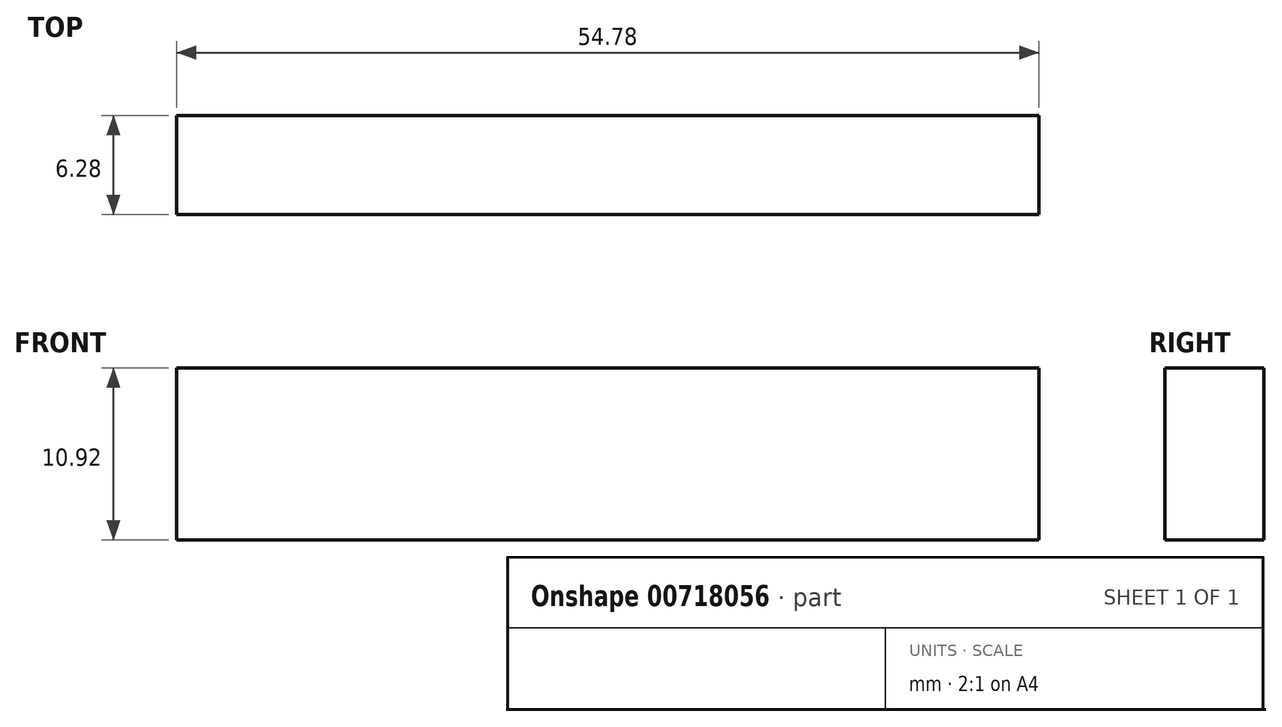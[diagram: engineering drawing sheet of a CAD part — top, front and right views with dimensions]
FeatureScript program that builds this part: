
annotation { "Feature Type Name" : "Feature", "Feature Type Description" : "" }
export const myFeature = defineFeature(function(context is Context, id is Id, definition is map)
    precondition{}
    {
        {
            var Q0;
            Q0=qCreatedBy(makeId("Front.planeOp"),FACE);
            var sketch = newSketch(context, id + "F0", { "sketchPlane" : qUnion([Q0])});
            skLineSegment(sketch, "E0.bottom", {"start": v(0, 0) * mm, "end": v(95.63, 0) * mm});
            skLineSegment(sketch, "E0.top", {"start": v(0, 97.83) * mm, "end": v(95.63, 97.83) * mm});
            skLineSegment(sketch, "E0.left", {"start": v(0, 0) * mm, "end": v(0, 97.83) * mm});
            skLineSegment(sketch, "E0.right", {"start": v(95.63, 0) * mm, "end": v(95.63, 97.83) * mm});
            skLineSegment(sketch, "E1.bottom", {"start": v(0, 97.83) * mm, "end": v(-94.65, 97.83) * mm});
            skLineSegment(sketch, "E1.top", {"start": v(0, -95.54) * mm, "end": v(-94.65, -95.54) * mm});
            skLineSegment(sketch, "E1.left", {"start": v(0, 97.83) * mm, "end": v(0, -95.54) * mm});
            skLineSegment(sketch, "E1.right", {"start": v(-94.65, 97.83) * mm, "end": v(-94.65, -95.54) * mm});
            skLineSegment(sketch, "E2.bottom", {"start": v(0, -95.54) * mm, "end": v(95.63, -95.54) * mm});
            skLineSegment(sketch, "E2.left", {"start": v(0, -95.54) * mm, "end": v(0, 0) * mm});
            skLineSegment(sketch, "E2.right", {"start": v(95.63, -95.54) * mm, "end": v(95.63, 0) * mm});
            skLineSegment(sketch, "E3.bottom", {"start": v(-34.5, 130.58) * mm, "end": v(16.55, 130.58) * mm});
            skLineSegment(sketch, "E3.top", {"start": v(-34.5, -108.24) * mm, "end": v(16.55, -108.24) * mm});
            skLineSegment(sketch, "E3.left", {"start": v(-34.5, 130.58) * mm, "end": v(-34.5, -108.24) * mm});
            skLineSegment(sketch, "E3.right", {"start": v(16.55, 130.58) * mm, "end": v(16.55, -108.24) * mm});
            skLineSegment(sketch, "E4.bottom", {"start": v(16.55, 130.58) * mm, "end": v(149.66, 130.58) * mm});
            skLineSegment(sketch, "E4.top", {"start": v(16.55, -99) * mm, "end": v(149.66, -99) * mm});
            skLineSegment(sketch, "E4.left", {"start": v(16.55, 130.58) * mm, "end": v(16.55, -99) * mm});
            skLineSegment(sketch, "E4.right", {"start": v(149.66, 130.58) * mm, "end": v(149.66, -99) * mm});
            skLineSegment(sketch, "E5.bottom", {"start": v(-34.5, -95.54) * mm, "end": v(-151.3, -95.54) * mm});
            skLineSegment(sketch, "E5.top", {"start": v(-34.5, 120.83) * mm, "end": v(-151.3, 120.83) * mm});
            skLineSegment(sketch, "E5.left", {"start": v(-34.5, -95.54) * mm, "end": v(-34.5, 120.83) * mm});
            skLineSegment(sketch, "E5.right", {"start": v(-151.3, -95.54) * mm, "end": v(-151.3, 120.83) * mm});
            skSolve(sketch);
        }
        {
            var Q0;
            Q0 = qSketchRegion(id + "F0", true);
            extrude(context, id + "F1", {"entities" : qUnion([Q0]), "depth" : 25.4 * mm, "offsetDistance" : 25.4 * mm});
        }
        {
            var Q0;
            Q0=makeQuery(id+"F1.opExtrude","CAP_FACE",FACE,{"disambiguationData":[OSD([sQuery(id+"F0.wireOp",EDGE,"E0.top"),sQuery(id+"F0.wireOp",EDGE,"E0.right"),sQuery(id+"F0.wireOp",EDGE,"E1.left"),sQuery(id+"F0.wireOp",EDGE,"E2.bottom"),sQuery(id+"F0.wireOp",EDGE,"E2.left"),sQuery(id+"F0.wireOp",EDGE,"E2.right"),sQuery(id+"F0.wireOp",EDGE,"E3.bottom"),sQuery(id+"F0.wireOp",EDGE,"E3.top"),sQuery(id+"F0.wireOp",EDGE,"E3.left"),sQuery(id+"F0.wireOp",EDGE,"E3.right"),sQuery(id+"F0.wireOp",EDGE,"E4.bottom"),sQuery(id+"F0.wireOp",EDGE,"E4.top"),sQuery(id+"F0.wireOp",EDGE,"E4.right"),sQuery(id+"F0.wireOp",EDGE,"E5.bottom"),sQuery(id+"F0.wireOp",EDGE,"E5.top"),sQuery(id+"F0.wireOp",EDGE,"E5.right")])],"isStart":true});
            var sketch = newSketch(context, id + "F2", { "sketchPlane" : qUnion([Q0])});
            skLineSegment(sketch, "E6.bottom", {"start": v(-95.63, 108.88) * mm, "end": v(291.77, 108.88) * mm});
            skLineSegment(sketch, "E6.top", {"start": v(-95.63, -277) * mm, "end": v(291.77, -277) * mm});
            skLineSegment(sketch, "E6.left", {"start": v(-95.63, 108.88) * mm, "end": v(-95.63, -277) * mm});
            skLineSegment(sketch, "E6.right", {"start": v(291.77, 108.88) * mm, "end": v(291.77, -277) * mm});
            skPoint(sketch, "E6.middle", {"position": v(98.07, -84.06) * mm});
            skSolve(sketch);
        }
        {
            var Q0;
            {var subQ13=makeQuery(id+"F1.opExtrude","CAP_EDGE",EDGE,{"disambiguationData":[OSD([sQuery(id+"F0.wireOp",EDGE,"E0.top")])],"isStart":true});Q0=makeQuery(id+"F2.imprint","IMPRINT",FACE,{"disambiguationData":[TD([[makeQuery(id+"F2.imprint","IMPRINT",EDGE,{"derivedFrom":subQ13}),-1.0]])]});}
            var Q1;
            {var subQ1=makeQuery(id+"F1.opExtrude","CAP_EDGE",EDGE,{"disambiguationData":[OSD([sQuery(id+"F0.wireOp",EDGE,"E0.top")])],"isStart":true});Q1=makeQuery(id+"F2.imprint","IMPRINT",FACE,{"disambiguationData":[TD([[makeQuery(id+"F2.imprint","IMPRINT",EDGE,{"derivedFrom":subQ1}),1.0]])]});}
            extrude(context, id + "F3", {"entities" : qUnion([Q0, Q1]), "operationType" : NewBodyOperationType.ADD, "oppositeDirection" : true, "depth" : 346.17 * mm, "offsetDistance" : 25.4 * mm});
        }
        {
            var Q0;
            {var subQ0=sQuery(id+"F0.wireOp",EDGE,"E5.right");var subQ1=sQuery(id+"F0.wireOp",EDGE,"E5.bottom");var subQ2=sQuery(id+"F0.wireOp",EDGE,"E4.top");var subQ3=sQuery(id+"F0.wireOp",EDGE,"E3.right");var subQ4=sQuery(id+"F0.wireOp",EDGE,"E3.left");var subQ5=sQuery(id+"F0.wireOp",EDGE,"E3.top");Q0=makeQuery(id+"F3.boolean.opBoolean","MERGE",FACE,{"derivedFrom":[makeQuery(id+"F1.opExtrude","CAP_FACE",FACE,{"disambiguationData":[OSD([sQuery(id+"F0.wireOp",EDGE,"E0.top"),sQuery(id+"F0.wireOp",EDGE,"E0.right"),sQuery(id+"F0.wireOp",EDGE,"E1.left"),sQuery(id+"F0.wireOp",EDGE,"E2.bottom"),sQuery(id+"F0.wireOp",EDGE,"E2.left"),sQuery(id+"F0.wireOp",EDGE,"E2.right"),sQuery(id+"F0.wireOp",EDGE,"E3.bottom"),subQ5,subQ4,subQ3,sQuery(id+"F0.wireOp",EDGE,"E4.bottom"),subQ2,sQuery(id+"F0.wireOp",EDGE,"E4.right"),subQ1,sQuery(id+"F0.wireOp",EDGE,"E5.top"),subQ0])],"isStart":true}),makeQuery(id+"F3.opExtrude","CAP_FACE",FACE,{"disambiguationData":[OSD([subQ5,subQ4,subQ3,subQ2,subQ1,subQ0,sQuery(id+"F2.wireOp",EDGE,"E6.bottom"),sQuery(id+"F2.wireOp",EDGE,"E6.left")])],"isStart":true})]});}
            var sketch = newSketch(context, id + "F4", { "sketchPlane" : qUnion([Q0])});
            skLineSegment(sketch, "E7.bottom", {"start": v(-77.36, 89.2) * mm, "end": v(78.88, 89.2) * mm});
            skLineSegment(sketch, "E7.top", {"start": v(-77.36, -67.08) * mm, "end": v(78.88, -67.08) * mm});
            skLineSegment(sketch, "E7.left", {"start": v(-77.36, 89.2) * mm, "end": v(-77.36, -67.08) * mm});
            skLineSegment(sketch, "E7.right", {"start": v(78.88, 89.2) * mm, "end": v(78.88, -67.08) * mm});
            skLineSegment(sketch, "E8.bottom", {"start": v(-113.4, 15.53) * mm, "end": v(-77.36, 15.53) * mm});
            skLineSegment(sketch, "E8.top", {"start": v(-113.4, 43.9) * mm, "end": v(-77.36, 43.9) * mm});
            skLineSegment(sketch, "E8.left", {"start": v(-113.4, 15.53) * mm, "end": v(-113.4, 43.9) * mm});
            skLineSegment(sketch, "E8.right", {"start": v(-77.36, 15.53) * mm, "end": v(-77.36, 43.9) * mm});
            skLineSegment(sketch, "E9.top", {"start": v(-113.4, -26.5) * mm, "end": v(-77.36, -26.5) * mm});
            skLineSegment(sketch, "E9.left", {"start": v(-113.4, 15.53) * mm, "end": v(-113.4, -26.5) * mm});
            skLineSegment(sketch, "E9.right", {"start": v(-77.36, 15.53) * mm, "end": v(-77.36, -26.5) * mm});
            skLineSegment(sketch, "E10.top", {"start": v(-113.4, -67.08) * mm, "end": v(-77.36, -67.08) * mm});
            skLineSegment(sketch, "E10.left", {"start": v(-113.4, -26.5) * mm, "end": v(-113.4, -67.08) * mm});
            skLineSegment(sketch, "E10.right", {"start": v(-77.36, -26.5) * mm, "end": v(-77.36, -67.08) * mm});
            skLineSegment(sketch, "E11.top", {"start": v(-113.4, 89.2) * mm, "end": v(-77.36, 89.2) * mm});
            skLineSegment(sketch, "E11.left", {"start": v(-113.4, 43.9) * mm, "end": v(-113.4, 89.2) * mm});
            skLineSegment(sketch, "E11.right", {"start": v(-77.36, 43.9) * mm, "end": v(-77.36, 89.2) * mm});
            skSolve(sketch);
        }
        {
            var Q0;
            Q0 = qSketchRegion(id + "F4", true);
            extrude(context, id + "F5", {"entities" : qUnion([Q0]), "operationType" : NewBodyOperationType.ADD, "depth" : 25.4 * mm, "offsetDistance" : 25.4 * mm});
        }
        {
            var Q0;
            Q0=makeQuery(id+"F5.opExtrude","CAP_FACE",FACE,{"disambiguationData":[OSD([sQuery(id+"F4.wireOp",EDGE,"E7.bottom"),sQuery(id+"F4.wireOp",EDGE,"E7.top"),sQuery(id+"F4.wireOp",EDGE,"E7.right"),sQuery(id+"F4.wireOp",EDGE,"E8.left"),sQuery(id+"F4.wireOp",EDGE,"E9.left"),sQuery(id+"F4.wireOp",EDGE,"E10.top"),sQuery(id+"F4.wireOp",EDGE,"E10.left"),sQuery(id+"F4.wireOp",EDGE,"E11.top"),sQuery(id+"F4.wireOp",EDGE,"E11.left")])],"isStart":false});
            var sketch = newSketch(context, id + "F6", { "sketchPlane" : qUnion([Q0])});
            skLineSegment(sketch, "E12.bottom", {"start": v(-94.88, 89.2) * mm, "end": v(78.88, 89.2) * mm});
            skLineSegment(sketch, "E12.top", {"start": v(-94.88, -67.08) * mm, "end": v(78.88, -67.08) * mm});
            skLineSegment(sketch, "E12.left", {"start": v(-94.88, 89.2) * mm, "end": v(-94.88, -67.08) * mm});
            skLineSegment(sketch, "E12.right", {"start": v(78.88, 89.2) * mm, "end": v(78.88, -67.08) * mm});
            skSolve(sketch);
        }
        {
            var Q0;
            Q0 = qSketchRegion(id + "F6", true);
            extrude(context, id + "F7", {"entities" : qUnion([Q0]), "operationType" : NewBodyOperationType.ADD, "depth" : 25.4 * mm, "offsetDistance" : 25.4 * mm});
        }
        {
            var Q0;
            Q0=makeQuery(id+"F7.opExtrude","SWEPT_FACE",FACE,{"disambiguationData":[OSD([sQuery(id+"F6.wireOp",EDGE,"E12.left")])]});
            var sketch = newSketch(context, id + "F8", { "sketchPlane" : qUnion([Q0])});
            skLineSegment(sketch, "E13.bottom", {"start": v(50.8, -67.08) * mm, "end": v(186.61, -67.08) * mm});
            skLineSegment(sketch, "E13.top", {"start": v(50.8, 89.35) * mm, "end": v(186.61, 89.35) * mm});
            skLineSegment(sketch, "E13.left", {"start": v(50.8, -67.08) * mm, "end": v(50.8, 89.35) * mm});
            skLineSegment(sketch, "E13.right", {"start": v(186.61, -67.08) * mm, "end": v(186.61, 89.35) * mm});
            skLineSegment(sketch, "E14.bottom", {"start": v(186.61, -67.08) * mm, "end": v(74.87, -67.08) * mm});
            skLineSegment(sketch, "E14.top", {"start": v(186.61, -85.28) * mm, "end": v(74.87, -85.28) * mm});
            skLineSegment(sketch, "E14.left", {"start": v(186.61, -67.08) * mm, "end": v(186.61, -85.28) * mm});
            skLineSegment(sketch, "E14.right", {"start": v(74.87, -67.08) * mm, "end": v(74.87, -85.28) * mm});
            skLineSegment(sketch, "E15.bottom", {"start": v(186.61, -67.08) * mm, "end": v(50.8, -67.08) * mm});
            skLineSegment(sketch, "E15.top", {"start": v(186.61, 89.35) * mm, "end": v(50.8, 89.35) * mm});
            skLineSegment(sketch, "E16.bottom", {"start": v(75.5, 70.37) * mm, "end": v(112.96, 70.37) * mm});
            skLineSegment(sketch, "E16.top", {"start": v(75.5, 100.12) * mm, "end": v(112.96, 100.12) * mm});
            skLineSegment(sketch, "E16.left", {"start": v(75.5, 70.37) * mm, "end": v(75.5, 100.12) * mm});
            skLineSegment(sketch, "E16.right", {"start": v(112.96, 70.37) * mm, "end": v(112.96, 100.12) * mm});
            skLineSegment(sketch, "E17.bottom", {"start": v(75.5, 100.12) * mm, "end": v(50.8, 100.12) * mm});
            skLineSegment(sketch, "E17.top", {"start": v(75.5, 89.2) * mm, "end": v(50.8, 89.2) * mm});
            skLineSegment(sketch, "E17.left", {"start": v(75.5, 100.12) * mm, "end": v(75.5, 89.2) * mm});
            skLineSegment(sketch, "E17.right", {"start": v(50.8, 100.12) * mm, "end": v(50.8, 89.2) * mm});
            skPoint(sketch, "E18.oppositeSnap0", {"position": v(38.1, 89.2) * mm});
            skLineSegment(sketch, "E18.bottom", {"start": v(50.8, 100.12) * mm, "end": v(-6.28, 100.12) * mm});
            skLineSegment(sketch, "E18.top", {"start": v(50.8, 89.2) * mm, "end": v(-6.28, 89.2) * mm});
            skLineSegment(sketch, "E18.right", {"start": v(-6.28, 100.12) * mm, "end": v(-6.28, 89.2) * mm});
            skSolve(sketch);
        }
        {
            var Q0;
            Q0 = qSketchRegion(id + "F8", true);
            extrude(context, id + "F9", {"entities" : qUnion([Q0]), "operationType" : NewBodyOperationType.INTERSECT, "depth" : 3015.54 * mm, "offsetDistance" : 25.4 * mm});
        }
    });
